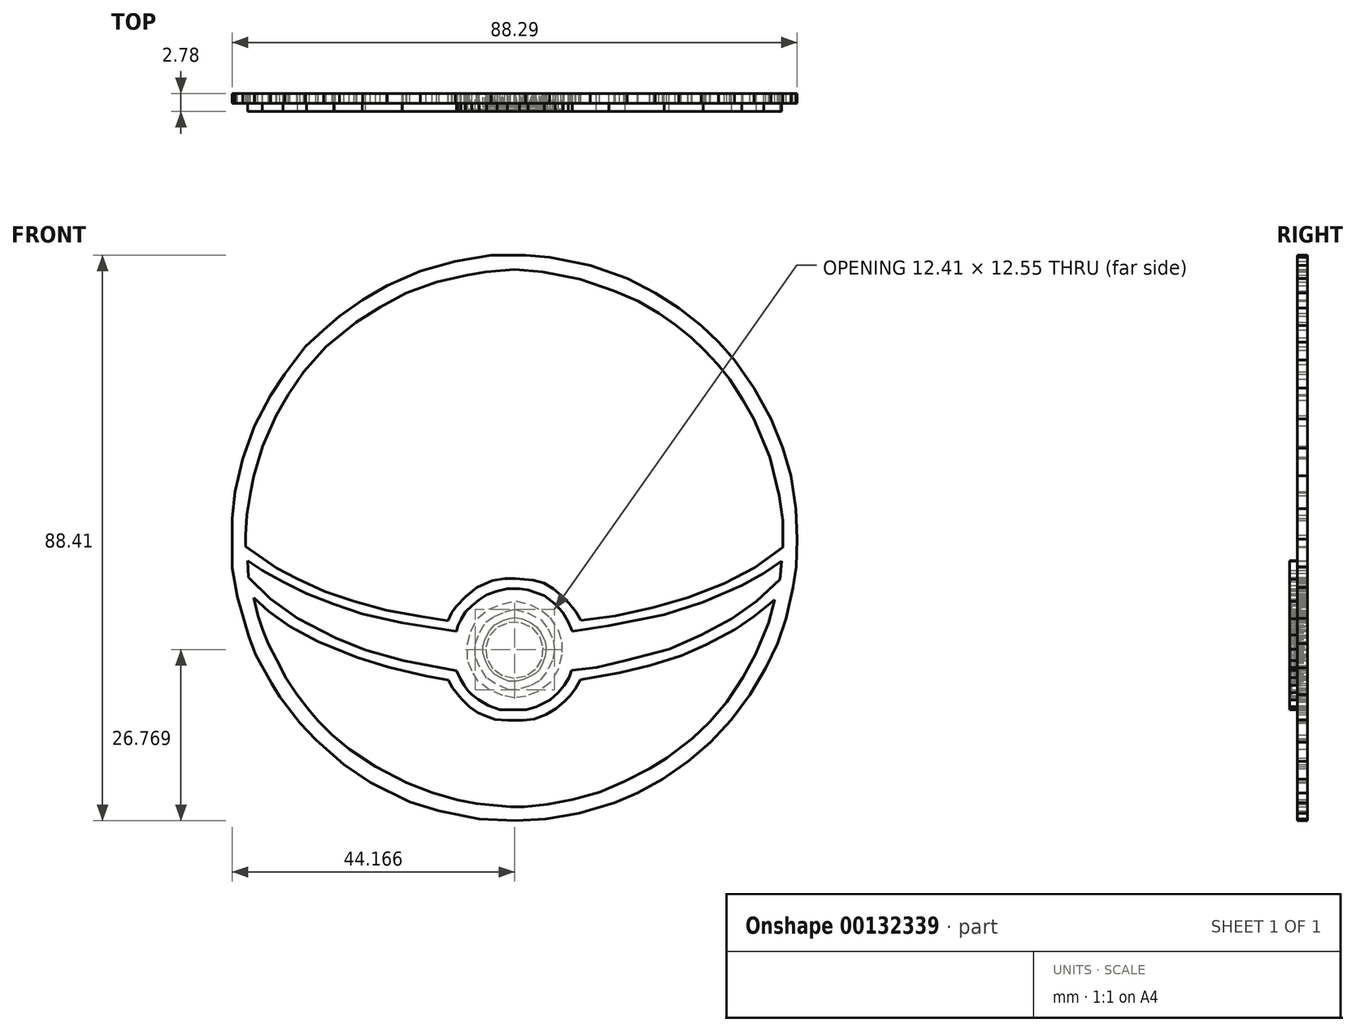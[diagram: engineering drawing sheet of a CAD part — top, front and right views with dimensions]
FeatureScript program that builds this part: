
annotation { "Feature Type Name" : "Feature", "Feature Type Description" : "" }
export const myFeature = defineFeature(function(context is Context, id is Id, definition is map)
    precondition{}
    {
        {
            var Q0;
            Q0=qCreatedBy(makeId("Front.planeOp"),FACE);
            var sketch = newSketch(context, id + "F0", { "sketchPlane" : qUnion([Q0])});
            skSolve(sketch);
        }
        {
            var Q0;
            Q0=qCreatedBy(makeId("Front.planeOp"),FACE);
            var sketch = newSketch(context, id + "F1", { "sketchPlane" : qUnion([Q0])});
            skLineSegment(sketch, "E0", {"start": v(0, 59.23) * mm, "end": v(4.43, 58.87) * mm});
            skLineSegment(sketch, "E1", {"start": v(4.43, 58.87) * mm, "end": v(10.26, 57.67) * mm});
            skLineSegment(sketch, "E2", {"start": v(10.26, 57.67) * mm, "end": v(15.6, 55.89) * mm});
            skLineSegment(sketch, "E3", {"start": v(15.6, 55.89) * mm, "end": v(19.35, 54.27) * mm});
            skLineSegment(sketch, "E4", {"start": v(19.35, 54.27) * mm, "end": v(22.58, 52.38) * mm});
            skLineSegment(sketch, "E5", {"start": v(22.58, 52.38) * mm, "end": v(25.1, 50.6) * mm});
            skLineSegment(sketch, "E6", {"start": v(25.1, 50.6) * mm, "end": v(27.64, 48.53) * mm});
            skLineSegment(sketch, "E7", {"start": v(27.64, 48.53) * mm, "end": v(29.66, 46.62) * mm});
            skLineSegment(sketch, "E8", {"start": v(29.66, 46.62) * mm, "end": v(31.76, 44.4) * mm});
            skLineSegment(sketch, "E9", {"start": v(31.76, 44.4) * mm, "end": v(33.61, 42.05) * mm});
            skLineSegment(sketch, "E10", {"start": v(33.61, 42.05) * mm, "end": v(35.72, 38.78) * mm});
            skLineSegment(sketch, "E11", {"start": v(35.72, 38.78) * mm, "end": v(37.4, 35.78) * mm});
            skLineSegment(sketch, "E12", {"start": v(37.4, 35.78) * mm, "end": v(39.9, 29.88) * mm});
            skLineSegment(sketch, "E13", {"start": v(39.9, 29.88) * mm, "end": v(41.39, 23.87) * mm});
            skLineSegment(sketch, "E14", {"start": v(41.39, 23.87) * mm, "end": v(41.94, 20) * mm});
            skLineSegment(sketch, "E15", {"start": v(41.94, 20) * mm, "end": v(41.94, 15.77) * mm});
            skLineSegment(sketch, "E16", {"start": v(41.94, 15.77) * mm, "end": v(37.54, 12.6) * mm});
            skLineSegment(sketch, "E17", {"start": v(37.54, 12.6) * mm, "end": v(32.78, 10.13) * mm});
            skLineSegment(sketch, "E18", {"start": v(32.78, 10.13) * mm, "end": v(27.08, 7.9) * mm});
            skLineSegment(sketch, "E19", {"start": v(27.08, 7.9) * mm, "end": v(21.76, 6.42) * mm});
            skLineSegment(sketch, "E20", {"start": v(21.76, 6.42) * mm, "end": v(15.78, 5.06) * mm});
            skLineSegment(sketch, "E21", {"start": v(15.78, 5.06) * mm, "end": v(10.37, 4.33) * mm});
            skLineSegment(sketch, "E22", {"start": v(10.37, 4.33) * mm, "end": v(9.6, 5.7) * mm});
            skLineSegment(sketch, "E23", {"start": v(9.6, 5.7) * mm, "end": v(8.54, 7.02) * mm});
            skLineSegment(sketch, "E24", {"start": v(8.54, 7.02) * mm, "end": v(7.27, 8.32) * mm});
            skLineSegment(sketch, "E25", {"start": v(7.27, 8.32) * mm, "end": v(6.05, 9.3) * mm});
            skLineSegment(sketch, "E26", {"start": v(6.05, 9.3) * mm, "end": v(4.6, 10.18) * mm});
            skLineSegment(sketch, "E27", {"start": v(4.6, 10.18) * mm, "end": v(2.97, 10.65) * mm});
            skLineSegment(sketch, "E28", {"start": v(2.97, 10.65) * mm, "end": v(0.17, 10.9) * mm});
            skLineSegment(sketch, "E29", {"start": v(0.17, 10.9) * mm, "end": v(-1.48, 10.9) * mm});
            skLineSegment(sketch, "E30", {"start": v(-1.48, 10.9) * mm, "end": v(-3.47, 10.6) * mm});
            skLineSegment(sketch, "E31", {"start": v(-3.47, 10.6) * mm, "end": v(-5.89, 9.5) * mm});
            skLineSegment(sketch, "E32", {"start": v(-5.89, 9.5) * mm, "end": v(-7.69, 8.06) * mm});
            skLineSegment(sketch, "E33", {"start": v(-7.69, 8.06) * mm, "end": v(-9.14, 6.52) * mm});
            skLineSegment(sketch, "E34", {"start": v(-9.14, 6.52) * mm, "end": v(-9.8, 5.6) * mm});
            skLineSegment(sketch, "E35", {"start": v(-9.8, 5.6) * mm, "end": v(-10.37, 4.27) * mm});
            skLineSegment(sketch, "E36", {"start": v(-10.37, 4.27) * mm, "end": v(-14.7, 5) * mm});
            skLineSegment(sketch, "E37", {"start": v(-14.7, 5) * mm, "end": v(-20.03, 5.94) * mm});
            skLineSegment(sketch, "E38", {"start": v(-20.03, 5.94) * mm, "end": v(-25.07, 7.37) * mm});
            skLineSegment(sketch, "E39", {"start": v(-25.07, 7.37) * mm, "end": v(-29.62, 8.85) * mm});
            skLineSegment(sketch, "E40", {"start": v(-29.62, 8.85) * mm, "end": v(-34, 10.88) * mm});
            skLineSegment(sketch, "E41", {"start": v(-34, 10.88) * mm, "end": v(-37.16, 12.57) * mm});
            skLineSegment(sketch, "E42", {"start": v(-37.16, 12.57) * mm, "end": v(-42.03, 15.9) * mm});
            skLineSegment(sketch, "E43", {"start": v(-42.03, 15.9) * mm, "end": v(-42.03, 17.66) * mm});
            skLineSegment(sketch, "E44", {"start": v(-42.03, 17.66) * mm, "end": v(-41.81, 20.8) * mm});
            skLineSegment(sketch, "E45", {"start": v(-41.81, 20.8) * mm, "end": v(-41.24, 24.28) * mm});
            skLineSegment(sketch, "E46", {"start": v(-41.24, 24.28) * mm, "end": v(-40.76, 26.91) * mm});
            skLineSegment(sketch, "E47", {"start": v(-40.76, 26.91) * mm, "end": v(-39.33, 31.62) * mm});
            skLineSegment(sketch, "E48", {"start": v(-39.33, 31.62) * mm, "end": v(-37.22, 36.36) * mm});
            skLineSegment(sketch, "E49", {"start": v(-37.22, 36.36) * mm, "end": v(-35.37, 39.64) * mm});
            skLineSegment(sketch, "E50", {"start": v(-35.37, 39.64) * mm, "end": v(-32.93, 43.2) * mm});
            skLineSegment(sketch, "E51", {"start": v(-32.93, 43.2) * mm, "end": v(-29.4, 47.18) * mm});
            skLineSegment(sketch, "E52", {"start": v(-29.4, 47.18) * mm, "end": v(-24.73, 50.99) * mm});
            skLineSegment(sketch, "E53", {"start": v(-24.73, 50.99) * mm, "end": v(-20.99, 53.3) * mm});
            skLineSegment(sketch, "E54", {"start": v(-20.99, 53.3) * mm, "end": v(-16.92, 55.53) * mm});
            skLineSegment(sketch, "E55", {"start": v(-16.92, 55.53) * mm, "end": v(-12.14, 57.27) * mm});
            skLineSegment(sketch, "E56", {"start": v(-12.14, 57.27) * mm, "end": v(-7.4, 58.35) * mm});
            skLineSegment(sketch, "E57", {"start": v(-7.4, 58.35) * mm, "end": v(-4.39, 58.84) * mm});
            skLineSegment(sketch, "E58", {"start": v(-4.39, 58.84) * mm, "end": v(0, 59.23) * mm});
            skSolve(sketch);
        }
        {
            var Q0;
            Q0=qCreatedBy(makeId("Front.planeOp"),FACE);
            var sketch = newSketch(context, id + "F2", { "sketchPlane" : qUnion([Q0])});
            skLineSegment(sketch, "E59", {"start": v(0.22, -26.97) * mm, "end": v(4.85, -26.67) * mm});
            skLineSegment(sketch, "E60", {"start": v(4.85, -26.67) * mm, "end": v(10.03, -25.83) * mm});
            skLineSegment(sketch, "E61", {"start": v(10.03, -25.83) * mm, "end": v(15.64, -24.13) * mm});
            skLineSegment(sketch, "E62", {"start": v(15.64, -24.13) * mm, "end": v(19.23, -22.62) * mm});
            skLineSegment(sketch, "E63", {"start": v(19.23, -22.62) * mm, "end": v(23.11, -20.5) * mm});
            skLineSegment(sketch, "E64", {"start": v(23.11, -20.5) * mm, "end": v(27.17, -17.7) * mm});
            skLineSegment(sketch, "E65", {"start": v(27.17, -17.7) * mm, "end": v(30.64, -14.68) * mm});
            skLineSegment(sketch, "E66", {"start": v(30.64, -14.68) * mm, "end": v(33.87, -11.18) * mm});
            skLineSegment(sketch, "E67", {"start": v(33.87, -11.18) * mm, "end": v(36.8, -7.24) * mm});
            skLineSegment(sketch, "E68", {"start": v(36.8, -7.24) * mm, "end": v(39.24, -3.08) * mm});
            skLineSegment(sketch, "E69", {"start": v(39.24, -3.08) * mm, "end": v(41.1, 0.7) * mm});
            skLineSegment(sketch, "E70", {"start": v(41.1, 0.7) * mm, "end": v(42.47, 4.7) * mm});
            skLineSegment(sketch, "E71", {"start": v(42.47, 4.7) * mm, "end": v(43.53, 9.49) * mm});
            skLineSegment(sketch, "E72", {"start": v(43.53, 9.49) * mm, "end": v(44, 12.77) * mm});
            skLineSegment(sketch, "E73", {"start": v(44, 12.77) * mm, "end": v(44.18, 17.08) * mm});
            skLineSegment(sketch, "E74", {"start": v(44.18, 17.08) * mm, "end": v(43.98, 21.84) * mm});
            skLineSegment(sketch, "E75", {"start": v(43.98, 21.84) * mm, "end": v(43.2, 26.96) * mm});
            skLineSegment(sketch, "E76", {"start": v(43.2, 26.96) * mm, "end": v(41.92, 31.29) * mm});
            skLineSegment(sketch, "E77", {"start": v(41.92, 31.29) * mm, "end": v(40.1, 35.85) * mm});
            skLineSegment(sketch, "E78", {"start": v(40.1, 35.85) * mm, "end": v(37.41, 40.68) * mm});
            skLineSegment(sketch, "E79", {"start": v(37.41, 40.68) * mm, "end": v(34.37, 45.07) * mm});
            skLineSegment(sketch, "E80", {"start": v(34.37, 45.07) * mm, "end": v(31.92, 47.86) * mm});
            skLineSegment(sketch, "E81", {"start": v(31.92, 47.86) * mm, "end": v(29.18, 50.46) * mm});
            skLineSegment(sketch, "E82", {"start": v(29.18, 50.46) * mm, "end": v(25.67, 53.22) * mm});
            skLineSegment(sketch, "E83", {"start": v(25.67, 53.22) * mm, "end": v(21.98, 55.54) * mm});
            skLineSegment(sketch, "E84", {"start": v(21.98, 55.54) * mm, "end": v(17.6, 57.85) * mm});
            skLineSegment(sketch, "E85", {"start": v(17.6, 57.85) * mm, "end": v(11.82, 59.83) * mm});
            skLineSegment(sketch, "E86", {"start": v(11.82, 59.83) * mm, "end": v(5.47, 61.12) * mm});
            skLineSegment(sketch, "E87", {"start": v(5.47, 61.12) * mm, "end": v(1.73, 61.44) * mm});
            skLineSegment(sketch, "E88", {"start": v(1.73, 61.44) * mm, "end": v(-3.64, 61.44) * mm});
            skLineSegment(sketch, "E89", {"start": v(-3.64, 61.44) * mm, "end": v(-9.26, 60.52) * mm});
            skLineSegment(sketch, "E90", {"start": v(-9.26, 60.52) * mm, "end": v(-14.7, 59) * mm});
            skLineSegment(sketch, "E91", {"start": v(-14.7, 59) * mm, "end": v(-19.91, 56.68) * mm});
            skLineSegment(sketch, "E92", {"start": v(-19.91, 56.68) * mm, "end": v(-23.72, 54.45) * mm});
            skLineSegment(sketch, "E93", {"start": v(-23.72, 54.45) * mm, "end": v(-27.33, 51.95) * mm});
            skLineSegment(sketch, "E94", {"start": v(-27.33, 51.95) * mm, "end": v(-29.83, 49.77) * mm});
            skLineSegment(sketch, "E95", {"start": v(-29.83, 49.77) * mm, "end": v(-32.66, 47.18) * mm});
            skLineSegment(sketch, "E96", {"start": v(-32.66, 47.18) * mm, "end": v(-35.91, 42.86) * mm});
            skLineSegment(sketch, "E97", {"start": v(-35.91, 42.86) * mm, "end": v(-38.16, 39.5) * mm});
            skLineSegment(sketch, "E98", {"start": v(-38.16, 39.5) * mm, "end": v(-40.63, 34.78) * mm});
            skLineSegment(sketch, "E99", {"start": v(-40.63, 34.78) * mm, "end": v(-42.45, 29.66) * mm});
            skLineSegment(sketch, "E100", {"start": v(-42.45, 29.66) * mm, "end": v(-43.63, 24.51) * mm});
            skLineSegment(sketch, "E101", {"start": v(-43.63, 24.51) * mm, "end": v(-44.11, 20.3) * mm});
            skLineSegment(sketch, "E102", {"start": v(-44.11, 20.3) * mm, "end": v(-44.11, 16.3) * mm});
            skLineSegment(sketch, "E103", {"start": v(-44.11, 16.3) * mm, "end": v(-44.11, 12.53) * mm});
            skLineSegment(sketch, "E104", {"start": v(-44.11, 12.53) * mm, "end": v(-43.3, 8) * mm});
            skLineSegment(sketch, "E105", {"start": v(-43.3, 8) * mm, "end": v(-41.53, 1.82) * mm});
            skLineSegment(sketch, "E106", {"start": v(-41.53, 1.82) * mm, "end": v(-40.44, -1.02) * mm});
            skLineSegment(sketch, "E107", {"start": v(-40.44, -1.02) * mm, "end": v(-37.97, -5.46) * mm});
            skLineSegment(sketch, "E108", {"start": v(-37.97, -5.46) * mm, "end": v(-36.66, -7.6) * mm});
            skLineSegment(sketch, "E109", {"start": v(-36.66, -7.6) * mm, "end": v(-33.52, -11.7) * mm});
            skLineSegment(sketch, "E110", {"start": v(-33.52, -11.7) * mm, "end": v(-31.06, -14.3) * mm});
            skLineSegment(sketch, "E111", {"start": v(-31.06, -14.3) * mm, "end": v(-26.65, -18.17) * mm});
            skLineSegment(sketch, "E112", {"start": v(-26.65, -18.17) * mm, "end": v(-22.5, -20.99) * mm});
            skLineSegment(sketch, "E113", {"start": v(-22.5, -20.99) * mm, "end": v(-16.33, -24.03) * mm});
            skLineSegment(sketch, "E114", {"start": v(-16.33, -24.03) * mm, "end": v(-11.8, -25.45) * mm});
            skLineSegment(sketch, "E115", {"start": v(-11.8, -25.45) * mm, "end": v(-5.48, -26.68) * mm});
            skLineSegment(sketch, "E116", {"start": v(-5.48, -26.68) * mm, "end": v(0.22, -26.97) * mm});
            skSolve(sketch);
        }
        {
            var Q0;
            Q0=makeQuery(id+"F2.imprint","IMPRINT",FACE,{"disambiguationData":[TD([[makeQuery(id+"F2.imprint","IMPRINT",EDGE,{"derivedFrom":sQuery(id+"F2.wireOp",EDGE,"E59")}),1.0]])]});
            var sketch = newSketch(context, id + "F3", { "sketchPlane" : qUnion([Q0])});
            skCircle(sketch, "E117.cCircle", {"center": v(0, -0.3) * mm, "radius": 4.36 * mm, "construction": true});
            skLineSegment(sketch, "E117.0", {"start": v(-0.06, -4.75) * mm, "end": v(-1.87, -4.34) * mm});
            skLineSegment(sketch, "E117.1", {"start": v(-1.87, -4.34) * mm, "end": v(-3.35, -3.23) * mm});
            skLineSegment(sketch, "E117.2", {"start": v(-3.35, -3.23) * mm, "end": v(-4.26, -1.61) * mm});
            skLineSegment(sketch, "E117.3", {"start": v(-4.26, -1.61) * mm, "end": v(-4.43, 0.23) * mm});
            skLineSegment(sketch, "E117.4", {"start": v(-4.43, 0.23) * mm, "end": v(-3.83, 1.99) * mm});
            skLineSegment(sketch, "E117.5", {"start": v(-3.83, 1.99) * mm, "end": v(-2.57, 3.35) * mm});
            skLineSegment(sketch, "E117.6", {"start": v(-2.57, 3.35) * mm, "end": v(-0.87, 4.08) * mm});
            skLineSegment(sketch, "E117.7", {"start": v(-0.87, 4.08) * mm, "end": v(0.99, 4.05) * mm});
            skLineSegment(sketch, "E117.8", {"start": v(0.99, 4.05) * mm, "end": v(2.67, 3.28) * mm});
            skLineSegment(sketch, "E117.9", {"start": v(2.67, 3.28) * mm, "end": v(3.9, 1.88) * mm});
            skLineSegment(sketch, "E117.10", {"start": v(3.9, 1.88) * mm, "end": v(4.44, 0.11) * mm});
            skLineSegment(sketch, "E117.11", {"start": v(4.44, 0.11) * mm, "end": v(4.22, -1.73) * mm});
            skLineSegment(sketch, "E117.12", {"start": v(4.22, -1.73) * mm, "end": v(3.27, -3.32) * mm});
            skLineSegment(sketch, "E117.13", {"start": v(3.27, -3.32) * mm, "end": v(1.76, -4.39) * mm});
            skLineSegment(sketch, "E117.14", {"start": v(1.76, -4.39) * mm, "end": v(-0.06, -4.75) * mm});
            skPoint(sketch, "E117.0.midPoint", {"position": v(-0.96, -4.55) * mm});
            skSolve(sketch);
        }
        {
            var Q0;
            Q0=makeQuery(id+"F2.imprint","IMPRINT",FACE,{"disambiguationData":[TD([[makeQuery(id+"F2.imprint","IMPRINT",EDGE,{"derivedFrom":sQuery(id+"F2.wireOp",EDGE,"E59")}),1.0]])]});
            var sketch = newSketch(context, id + "F4", { "sketchPlane" : qUnion([Q0])});
            skLineSegment(sketch, "E118", {"start": v(0.09, 4.83) * mm, "end": v(1.22, 4.6) * mm});
            skLineSegment(sketch, "E119", {"start": v(1.22, 4.6) * mm, "end": v(2.54, 4) * mm});
            skLineSegment(sketch, "E120", {"start": v(2.54, 4) * mm, "end": v(3.47, 3.33) * mm});
            skLineSegment(sketch, "E121", {"start": v(3.47, 3.33) * mm, "end": v(4.15, 2.39) * mm});
            skLineSegment(sketch, "E122", {"start": v(4.15, 2.39) * mm, "end": v(4.77, 1.08) * mm});
            skLineSegment(sketch, "E123", {"start": v(4.77, 1.08) * mm, "end": v(4.94, 0.25) * mm});
            skLineSegment(sketch, "E124", {"start": v(4.94, 0.25) * mm, "end": v(4.94, -0.45) * mm});
            skLineSegment(sketch, "E125", {"start": v(4.94, -0.45) * mm, "end": v(4.79, -1.23) * mm});
            skLineSegment(sketch, "E126", {"start": v(4.79, -1.23) * mm, "end": v(4.38, -2.32) * mm});
            skLineSegment(sketch, "E127", {"start": v(4.38, -2.32) * mm, "end": v(3.88, -3.4) * mm});
            skLineSegment(sketch, "E128", {"start": v(3.88, -3.4) * mm, "end": v(3.3, -3.93) * mm});
            skLineSegment(sketch, "E129", {"start": v(3.3, -3.93) * mm, "end": v(2.58, -4.34) * mm});
            skLineSegment(sketch, "E130", {"start": v(2.58, -4.34) * mm, "end": v(1.34, -4.93) * mm});
            skLineSegment(sketch, "E131", {"start": v(1.34, -4.93) * mm, "end": v(0.32, -5.15) * mm});
            skLineSegment(sketch, "E132", {"start": v(0.32, -5.15) * mm, "end": v(-0.92, -5.15) * mm});
            skLineSegment(sketch, "E133", {"start": v(-0.92, -5.15) * mm, "end": v(-2.02, -4.66) * mm});
            skLineSegment(sketch, "E134", {"start": v(-2.02, -4.66) * mm, "end": v(-3.1, -4.08) * mm});
            skLineSegment(sketch, "E135", {"start": v(-3.1, -4.08) * mm, "end": v(-3.92, -3.2) * mm});
            skLineSegment(sketch, "E136", {"start": v(-3.92, -3.2) * mm, "end": v(-4.5, -2.06) * mm});
            skLineSegment(sketch, "E137", {"start": v(-4.5, -2.06) * mm, "end": v(-4.95, -0.73) * mm});
            skLineSegment(sketch, "E138", {"start": v(-4.95, -0.73) * mm, "end": v(-4.95, 0.37) * mm});
            skLineSegment(sketch, "E139", {"start": v(-4.95, 0.37) * mm, "end": v(-4.6, 1.4) * mm});
            skLineSegment(sketch, "E140", {"start": v(-4.6, 1.4) * mm, "end": v(-3.93, 2.73) * mm});
            skLineSegment(sketch, "E141", {"start": v(-3.93, 2.73) * mm, "end": v(-3.08, 3.69) * mm});
            skLineSegment(sketch, "E142", {"start": v(-3.08, 3.69) * mm, "end": v(-1.77, 4.34) * mm});
            skLineSegment(sketch, "E143", {"start": v(-1.77, 4.34) * mm, "end": v(-0.73, 4.7) * mm});
            skLineSegment(sketch, "E144", {"start": v(-0.73, 4.7) * mm, "end": v(0.09, 4.83) * mm});
            skSolve(sketch);
        }
        {
            var Q0;
            Q0=makeQuery(id+"F2.imprint","IMPRINT",FACE,{"disambiguationData":[TD([[makeQuery(id+"F2.imprint","IMPRINT",EDGE,{"derivedFrom":sQuery(id+"F2.wireOp",EDGE,"E59")}),1.0]])]});
            var sketch = newSketch(context, id + "F5", { "sketchPlane" : qUnion([Q0])});
            skLineSegment(sketch, "E145", {"start": v(0, 6.08) * mm, "end": v(2.02, 5.54) * mm});
            skLineSegment(sketch, "E146", {"start": v(2.02, 5.54) * mm, "end": v(4.14, 4.46) * mm});
            skLineSegment(sketch, "E147", {"start": v(4.14, 4.46) * mm, "end": v(5.21, 3.08) * mm});
            skLineSegment(sketch, "E148", {"start": v(5.21, 3.08) * mm, "end": v(6.06, 1.27) * mm});
            skLineSegment(sketch, "E149", {"start": v(6.06, 1.27) * mm, "end": v(6.26, -0.23) * mm});
            skLineSegment(sketch, "E150", {"start": v(6.26, -0.23) * mm, "end": v(5.92, -1.93) * mm});
            skLineSegment(sketch, "E151", {"start": v(5.92, -1.93) * mm, "end": v(4.96, -3.8) * mm});
            skLineSegment(sketch, "E152", {"start": v(4.96, -3.8) * mm, "end": v(3.89, -5.1) * mm});
            skLineSegment(sketch, "E153", {"start": v(3.89, -5.1) * mm, "end": v(2.42, -5.85) * mm});
            skLineSegment(sketch, "E154", {"start": v(2.42, -5.85) * mm, "end": v(0.38, -6.48) * mm});
            skLineSegment(sketch, "E155", {"start": v(0.38, -6.48) * mm, "end": v(-0.92, -6.48) * mm});
            skLineSegment(sketch, "E156", {"start": v(-0.92, -6.48) * mm, "end": v(-2.95, -5.52) * mm});
            skLineSegment(sketch, "E157", {"start": v(-2.95, -5.52) * mm, "end": v(-4.34, -4.67) * mm});
            skLineSegment(sketch, "E158", {"start": v(-4.34, -4.67) * mm, "end": v(-5.41, -2.97) * mm});
            skLineSegment(sketch, "E159", {"start": v(-5.41, -2.97) * mm, "end": v(-6.15, -1.16) * mm});
            skLineSegment(sketch, "E160", {"start": v(-6.15, -1.16) * mm, "end": v(-6.15, 0.65) * mm});
            skLineSegment(sketch, "E161", {"start": v(-6.15, 0.65) * mm, "end": v(-5.41, 2.49) * mm});
            skLineSegment(sketch, "E162", {"start": v(-5.41, 2.49) * mm, "end": v(-4.45, 4.12) * mm});
            skLineSegment(sketch, "E163", {"start": v(-4.45, 4.12) * mm, "end": v(-3.1, 5) * mm});
            skLineSegment(sketch, "E164", {"start": v(-3.1, 5) * mm, "end": v(-1.51, 5.68) * mm});
            skLineSegment(sketch, "E165", {"start": v(-1.51, 5.68) * mm, "end": v(0, 6.08) * mm});
            skLineSegment(sketch, "E166", {"start": v(0.21, 7.4) * mm, "end": v(2.42, 6.81) * mm});
            skLineSegment(sketch, "E167", {"start": v(2.42, 6.81) * mm, "end": v(4.31, 5.88) * mm});
            skLineSegment(sketch, "E168", {"start": v(4.31, 5.88) * mm, "end": v(5.53, 4.83) * mm});
            skLineSegment(sketch, "E169", {"start": v(5.53, 4.83) * mm, "end": v(6.8, 2.85) * mm});
            skLineSegment(sketch, "E170", {"start": v(6.8, 2.85) * mm, "end": v(7.42, 0.93) * mm});
            skLineSegment(sketch, "E171", {"start": v(7.42, 0.93) * mm, "end": v(7.42, -1.05) * mm});
            skLineSegment(sketch, "E172", {"start": v(7.42, -1.05) * mm, "end": v(6.85, -3.23) * mm});
            skLineSegment(sketch, "E173", {"start": v(6.85, -3.23) * mm, "end": v(5.61, -5.35) * mm});
            skLineSegment(sketch, "E174", {"start": v(5.61, -5.35) * mm, "end": v(3.6, -6.79) * mm});
            skLineSegment(sketch, "E175", {"start": v(3.6, -6.79) * mm, "end": v(1.8, -7.5) * mm});
            skLineSegment(sketch, "E176", {"start": v(1.8, -7.5) * mm, "end": v(0, -7.78) * mm});
            skLineSegment(sketch, "E177", {"start": v(0, -7.78) * mm, "end": v(-1.8, -7.4) * mm});
            skLineSegment(sketch, "E178", {"start": v(-1.8, -7.4) * mm, "end": v(-3.86, -6.53) * mm});
            skLineSegment(sketch, "E179", {"start": v(-3.86, -6.53) * mm, "end": v(-5.67, -5.15) * mm});
            skLineSegment(sketch, "E180", {"start": v(-5.67, -5.15) * mm, "end": v(-6.63, -3.6) * mm});
            skLineSegment(sketch, "E181", {"start": v(-6.63, -3.6) * mm, "end": v(-7.36, -1.73) * mm});
            skLineSegment(sketch, "E182", {"start": v(-7.36, -1.73) * mm, "end": v(-7.36, 0.7) * mm});
            skLineSegment(sketch, "E183", {"start": v(-7.36, 0.7) * mm, "end": v(-6.83, 2.63) * mm});
            skLineSegment(sketch, "E184", {"start": v(-6.83, 2.63) * mm, "end": v(-5.7, 4.75) * mm});
            skLineSegment(sketch, "E185", {"start": v(-5.7, 4.75) * mm, "end": v(-3.97, 6.13) * mm});
            skLineSegment(sketch, "E186", {"start": v(-3.97, 6.13) * mm, "end": v(-1.9, 6.92) * mm});
            skLineSegment(sketch, "E187", {"start": v(-1.9, 6.92) * mm, "end": v(0.21, 7.4) * mm});
            skSolve(sketch);
        }
        {
            var Q0;
            Q0=makeQuery(id+"F2.imprint","IMPRINT",FACE,{"disambiguationData":[TD([[makeQuery(id+"F2.imprint","IMPRINT",EDGE,{"derivedFrom":sQuery(id+"F2.wireOp",EDGE,"E59")}),1.0]])]});
            var sketch = newSketch(context, id + "F6", { "sketchPlane" : qUnion([Q0])});
            skLineSegment(sketch, "E188", {"start": v(-41.7, 13.72) * mm, "end": v(-41.59, 11.07) * mm});
            skLineSegment(sketch, "E189", {"start": v(-41.59, 11.07) * mm, "end": v(-38.17, 7.72) * mm});
            skLineSegment(sketch, "E190", {"start": v(-38.17, 7.72) * mm, "end": v(-33.89, 4.65) * mm});
            skLineSegment(sketch, "E191", {"start": v(-33.89, 4.65) * mm, "end": v(-27.98, 1.65) * mm});
            skLineSegment(sketch, "E192", {"start": v(-27.98, 1.65) * mm, "end": v(-23.27, -0.27) * mm});
            skLineSegment(sketch, "E193", {"start": v(-23.27, -0.27) * mm, "end": v(-17.34, -1.92) * mm});
            skLineSegment(sketch, "E194", {"start": v(-17.34, -1.92) * mm, "end": v(-9.05, -3.54) * mm});
            skLineSegment(sketch, "E195", {"start": v(-9.05, -3.54) * mm, "end": v(-8.48, -4.73) * mm});
            skLineSegment(sketch, "E196", {"start": v(-8.48, -4.73) * mm, "end": v(-7.84, -5.83) * mm});
            skLineSegment(sketch, "E197", {"start": v(-7.84, -5.83) * mm, "end": v(-7.26, -6.6) * mm});
            skLineSegment(sketch, "E198", {"start": v(-7.26, -6.6) * mm, "end": v(-6.62, -7.25) * mm});
            skLineSegment(sketch, "E199", {"start": v(-6.62, -7.25) * mm, "end": v(-5.65, -8) * mm});
            skLineSegment(sketch, "E200", {"start": v(-5.65, -8) * mm, "end": v(-4.06, -8.97) * mm});
            skLineSegment(sketch, "E201", {"start": v(-4.06, -8.97) * mm, "end": v(-2.25, -9.59) * mm});
            skLineSegment(sketch, "E202", {"start": v(-2.25, -9.59) * mm, "end": v(1.8, -9.59) * mm});
            skLineSegment(sketch, "E203", {"start": v(1.8, -9.59) * mm, "end": v(3.4, -9.16) * mm});
            skLineSegment(sketch, "E204", {"start": v(3.4, -9.16) * mm, "end": v(5.55, -8.1) * mm});
            skLineSegment(sketch, "E205", {"start": v(5.55, -8.1) * mm, "end": v(6.84, -6.96) * mm});
            skLineSegment(sketch, "E206", {"start": v(6.84, -6.96) * mm, "end": v(7.76, -5.83) * mm});
            skLineSegment(sketch, "E207", {"start": v(7.76, -5.83) * mm, "end": v(8.53, -4.58) * mm});
            skLineSegment(sketch, "E208", {"start": v(8.53, -4.58) * mm, "end": v(8.93, -3.45) * mm});
            skLineSegment(sketch, "E209", {"start": v(8.93, -3.45) * mm, "end": v(12.78, -2.98) * mm});
            skLineSegment(sketch, "E210", {"start": v(12.78, -2.98) * mm, "end": v(17.3, -1.9) * mm});
            skLineSegment(sketch, "E211", {"start": v(17.3, -1.9) * mm, "end": v(24.15, -0.16) * mm});
            skLineSegment(sketch, "E212", {"start": v(24.15, -0.16) * mm, "end": v(29.16, 2.05) * mm});
            skLineSegment(sketch, "E213", {"start": v(29.16, 2.05) * mm, "end": v(33.93, 4.64) * mm});
            skLineSegment(sketch, "E214", {"start": v(33.93, 4.64) * mm, "end": v(37.83, 7.33) * mm});
            skLineSegment(sketch, "E215", {"start": v(37.83, 7.33) * mm, "end": v(41.47, 10.74) * mm});
            skLineSegment(sketch, "E216", {"start": v(41.47, 10.74) * mm, "end": v(41.77, 13.62) * mm});
            skLineSegment(sketch, "E217", {"start": v(41.77, 13.62) * mm, "end": v(38.95, 11.74) * mm});
            skLineSegment(sketch, "E218", {"start": v(38.95, 11.74) * mm, "end": v(35.53, 9.84) * mm});
            skLineSegment(sketch, "E219", {"start": v(35.53, 9.84) * mm, "end": v(29.49, 7.22) * mm});
            skLineSegment(sketch, "E220", {"start": v(29.49, 7.22) * mm, "end": v(23.42, 5.24) * mm});
            skLineSegment(sketch, "E221", {"start": v(23.42, 5.24) * mm, "end": v(14.74, 3.52) * mm});
            skLineSegment(sketch, "E222", {"start": v(14.74, 3.52) * mm, "end": v(9.03, 2.63) * mm});
            skLineSegment(sketch, "E223", {"start": v(9.03, 2.63) * mm, "end": v(8.4, 4.07) * mm});
            skLineSegment(sketch, "E224", {"start": v(8.4, 4.07) * mm, "end": v(7.57, 5.56) * mm});
            skLineSegment(sketch, "E225", {"start": v(7.57, 5.56) * mm, "end": v(6.38, 6.88) * mm});
            skLineSegment(sketch, "E226", {"start": v(6.38, 6.88) * mm, "end": v(4.66, 8.23) * mm});
            skLineSegment(sketch, "E227", {"start": v(4.66, 8.23) * mm, "end": v(2.14, 9.14) * mm});
            skLineSegment(sketch, "E228", {"start": v(2.14, 9.14) * mm, "end": v(0.8, 9.3) * mm});
            skLineSegment(sketch, "E229", {"start": v(0.8, 9.3) * mm, "end": v(-1.13, 9.3) * mm});
            skLineSegment(sketch, "E230", {"start": v(-1.13, 9.3) * mm, "end": v(-2.69, 8.9) * mm});
            skLineSegment(sketch, "E231", {"start": v(-2.69, 8.9) * mm, "end": v(-4.35, 8.34) * mm});
            skLineSegment(sketch, "E232", {"start": v(-4.35, 8.34) * mm, "end": v(-5.5, 7.62) * mm});
            skLineSegment(sketch, "E233", {"start": v(-5.5, 7.62) * mm, "end": v(-6.67, 6.67) * mm});
            skLineSegment(sketch, "E234", {"start": v(-6.67, 6.67) * mm, "end": v(-7.66, 5.66) * mm});
            skLineSegment(sketch, "E235", {"start": v(-7.66, 5.66) * mm, "end": v(-8.35, 4.5) * mm});
            skLineSegment(sketch, "E236", {"start": v(-8.35, 4.5) * mm, "end": v(-8.88, 3.47) * mm});
            skLineSegment(sketch, "E237", {"start": v(-8.88, 3.47) * mm, "end": v(-9.07, 2.67) * mm});
            skLineSegment(sketch, "E238", {"start": v(-9.07, 2.67) * mm, "end": v(-13.15, 3.29) * mm});
            skLineSegment(sketch, "E239", {"start": v(-13.15, 3.29) * mm, "end": v(-17.55, 3.97) * mm});
            skLineSegment(sketch, "E240", {"start": v(-17.55, 3.97) * mm, "end": v(-23.78, 5.36) * mm});
            skLineSegment(sketch, "E241", {"start": v(-23.78, 5.36) * mm, "end": v(-28.25, 6.9) * mm});
            skLineSegment(sketch, "E242", {"start": v(-28.25, 6.9) * mm, "end": v(-32.46, 8.58) * mm});
            skLineSegment(sketch, "E243", {"start": v(-32.46, 8.58) * mm, "end": v(-36.18, 10.4) * mm});
            skLineSegment(sketch, "E244", {"start": v(-36.18, 10.4) * mm, "end": v(-39.4, 12.18) * mm});
            skLineSegment(sketch, "E245", {"start": v(-39.4, 12.18) * mm, "end": v(-41.7, 13.72) * mm});
            skSolve(sketch);
        }
        {
            var Q0;
            Q0=makeQuery(id+"F2.imprint","IMPRINT",FACE,{"disambiguationData":[TD([[makeQuery(id+"F2.imprint","IMPRINT",EDGE,{"derivedFrom":sQuery(id+"F2.wireOp",EDGE,"E59")}),1.0]])]});
            var sketch = newSketch(context, id + "F7", { "sketchPlane" : qUnion([Q0])});
            skLineSegment(sketch, "E246", {"start": v(-40.74, 7.9) * mm, "end": v(-40.1, 5.18) * mm});
            skLineSegment(sketch, "E247", {"start": v(-40.1, 5.18) * mm, "end": v(-39.35, 2.9) * mm});
            skLineSegment(sketch, "E248", {"start": v(-39.35, 2.9) * mm, "end": v(-38.45, 0.7) * mm});
            skLineSegment(sketch, "E249", {"start": v(-38.45, 0.7) * mm, "end": v(-37.15, -1.89) * mm});
            skLineSegment(sketch, "E250", {"start": v(-37.15, -1.89) * mm, "end": v(-35.63, -4.74) * mm});
            skLineSegment(sketch, "E251", {"start": v(-35.63, -4.74) * mm, "end": v(-34, -7.2) * mm});
            skLineSegment(sketch, "E252", {"start": v(-34, -7.2) * mm, "end": v(-32.07, -9.72) * mm});
            skLineSegment(sketch, "E253", {"start": v(-32.07, -9.72) * mm, "end": v(-30.64, -11.36) * mm});
            skLineSegment(sketch, "E254", {"start": v(-30.64, -11.36) * mm, "end": v(-28.45, -13.56) * mm});
            skLineSegment(sketch, "E255", {"start": v(-28.45, -13.56) * mm, "end": v(-25.79, -15.8) * mm});
            skLineSegment(sketch, "E256", {"start": v(-25.79, -15.8) * mm, "end": v(-21.72, -18.48) * mm});
            skLineSegment(sketch, "E257", {"start": v(-21.72, -18.48) * mm, "end": v(-16.82, -21.03) * mm});
            skLineSegment(sketch, "E258", {"start": v(-16.82, -21.03) * mm, "end": v(-12.84, -22.55) * mm});
            skLineSegment(sketch, "E259", {"start": v(-12.84, -22.55) * mm, "end": v(-8.93, -23.7) * mm});
            skLineSegment(sketch, "E260", {"start": v(-8.93, -23.7) * mm, "end": v(-5.94, -24.28) * mm});
            skLineSegment(sketch, "E261", {"start": v(-5.94, -24.28) * mm, "end": v(-2.61, -24.6) * mm});
            skLineSegment(sketch, "E262", {"start": v(-2.61, -24.6) * mm, "end": v(-0.6, -24.8) * mm});
            skLineSegment(sketch, "E263", {"start": v(-0.6, -24.8) * mm, "end": v(1.54, -24.8) * mm});
            skLineSegment(sketch, "E264", {"start": v(1.54, -24.8) * mm, "end": v(5.12, -24.4) * mm});
            skLineSegment(sketch, "E265", {"start": v(5.12, -24.4) * mm, "end": v(9.1, -23.65) * mm});
            skLineSegment(sketch, "E266", {"start": v(9.1, -23.65) * mm, "end": v(13.32, -22.5) * mm});
            skLineSegment(sketch, "E267", {"start": v(13.32, -22.5) * mm, "end": v(17.08, -20.88) * mm});
            skLineSegment(sketch, "E268", {"start": v(17.08, -20.88) * mm, "end": v(21.14, -18.8) * mm});
            skLineSegment(sketch, "E269", {"start": v(21.14, -18.8) * mm, "end": v(23.8, -17.16) * mm});
            skLineSegment(sketch, "E270", {"start": v(23.8, -17.16) * mm, "end": v(27.75, -14.1) * mm});
            skLineSegment(sketch, "E271", {"start": v(27.75, -14.1) * mm, "end": v(30.51, -11.53) * mm});
            skLineSegment(sketch, "E272", {"start": v(30.51, -11.53) * mm, "end": v(33.18, -8.4) * mm});
            skLineSegment(sketch, "E273", {"start": v(33.18, -8.4) * mm, "end": v(35.7, -4.54) * mm});
            skLineSegment(sketch, "E274", {"start": v(35.7, -4.54) * mm, "end": v(37.69, -0.94) * mm});
            skLineSegment(sketch, "E275", {"start": v(37.69, -0.94) * mm, "end": v(39.72, 3.97) * mm});
            skLineSegment(sketch, "E276", {"start": v(39.72, 3.97) * mm, "end": v(40.7, 7.58) * mm});
            skLineSegment(sketch, "E277", {"start": v(40.7, 7.58) * mm, "end": v(39.28, 6.48) * mm});
            skLineSegment(sketch, "E278", {"start": v(39.28, 6.48) * mm, "end": v(37.36, 4.93) * mm});
            skLineSegment(sketch, "E279", {"start": v(37.36, 4.93) * mm, "end": v(34.5, 3) * mm});
            skLineSegment(sketch, "E280", {"start": v(34.5, 3) * mm, "end": v(29.95, 0.58) * mm});
            skLineSegment(sketch, "E281", {"start": v(29.95, 0.58) * mm, "end": v(26.07, -1.13) * mm});
            skLineSegment(sketch, "E282", {"start": v(26.07, -1.13) * mm, "end": v(21.15, -2.68) * mm});
            skLineSegment(sketch, "E283", {"start": v(21.15, -2.68) * mm, "end": v(16.43, -3.83) * mm});
            skLineSegment(sketch, "E284", {"start": v(16.43, -3.83) * mm, "end": v(10.29, -4.88) * mm});
            skLineSegment(sketch, "E285", {"start": v(10.29, -4.88) * mm, "end": v(9.5, -6.35) * mm});
            skLineSegment(sketch, "E286", {"start": v(9.5, -6.35) * mm, "end": v(8.65, -7.43) * mm});
            skLineSegment(sketch, "E287", {"start": v(8.65, -7.43) * mm, "end": v(7.79, -8.35) * mm});
            skLineSegment(sketch, "E288", {"start": v(7.79, -8.35) * mm, "end": v(6.48, -9.44) * mm});
            skLineSegment(sketch, "E289", {"start": v(6.48, -9.44) * mm, "end": v(4.92, -10.37) * mm});
            skLineSegment(sketch, "E290", {"start": v(4.92, -10.37) * mm, "end": v(3.08, -11.07) * mm});
            skLineSegment(sketch, "E291", {"start": v(3.08, -11.07) * mm, "end": v(1.35, -11.24) * mm});
            skLineSegment(sketch, "E292", {"start": v(1.35, -11.24) * mm, "end": v(-1.04, -11.24) * mm});
            skLineSegment(sketch, "E293", {"start": v(-1.04, -11.24) * mm, "end": v(-3.05, -11.13) * mm});
            skLineSegment(sketch, "E294", {"start": v(-3.05, -11.13) * mm, "end": v(-4.56, -10.55) * mm});
            skLineSegment(sketch, "E295", {"start": v(-4.56, -10.55) * mm, "end": v(-5.74, -10.08) * mm});
            skLineSegment(sketch, "E296", {"start": v(-5.74, -10.08) * mm, "end": v(-7.04, -9.17) * mm});
            skLineSegment(sketch, "E297", {"start": v(-7.04, -9.17) * mm, "end": v(-8.26, -7.92) * mm});
            skLineSegment(sketch, "E298", {"start": v(-8.26, -7.92) * mm, "end": v(-9.72, -6.15) * mm});
            skLineSegment(sketch, "E299", {"start": v(-9.72, -6.15) * mm, "end": v(-10.3, -4.95) * mm});
            skLineSegment(sketch, "E300", {"start": v(-10.3, -4.95) * mm, "end": v(-13.8, -4.33) * mm});
            skLineSegment(sketch, "E301", {"start": v(-13.8, -4.33) * mm, "end": v(-19.75, -2.94) * mm});
            skLineSegment(sketch, "E302", {"start": v(-19.75, -2.94) * mm, "end": v(-24.63, -1.4) * mm});
            skLineSegment(sketch, "E303", {"start": v(-24.63, -1.4) * mm, "end": v(-30.72, 1.03) * mm});
            skLineSegment(sketch, "E304", {"start": v(-30.72, 1.03) * mm, "end": v(-35.1, 3.43) * mm});
            skLineSegment(sketch, "E305", {"start": v(-35.1, 3.43) * mm, "end": v(-38.38, 5.75) * mm});
            skLineSegment(sketch, "E306", {"start": v(-38.38, 5.75) * mm, "end": v(-40.74, 7.9) * mm});
            skSolve(sketch);
        }
        {
            var Q0;
            Q0 = qSketchRegion(id + "F0", true);
            var Q1;
            Q1 = qSketchRegion(id + "F1", true);
            var Q2;
            Q2 = qSketchRegion(id + "F2", true);
            var Q3;
            Q3 = qSketchRegion(id + "F6", true);
            var Q4;
            Q4 = qSketchRegion(id + "F7", true);
            extrude(context, id + "F8", {"entities" : qUnion([Q0, Q1, Q2, Q3, Q4]), "depth" : 1.56 * mm});
        }
        {
            var Q0;
            Q0 = qSketchRegion(id + "F3", true);
            extrude(context, id + "F9", {"entities" : qUnion([Q0]), "depth" : 1.84 * mm});
        }
        {
            var Q0;
            Q0 = qSketchRegion(id + "F4", true);
            extrude(context, id + "F10", {"entities" : qUnion([Q0]), "depth" : 2.09 * mm});
        }
        {
            var Q0;
            Q0 = qSketchRegion(id + "F5", true);
            extrude(context, id + "F11", {"entities" : qUnion([Q0]), "depth" : 2.45 * mm});
        }
        {
            var Q0;
            Q0 = qSketchRegion(id + "F6", true);
            extrude(context, id + "F12", {"entities" : qUnion([Q0]), "depth" : 2.78 * mm});
        }
    });
